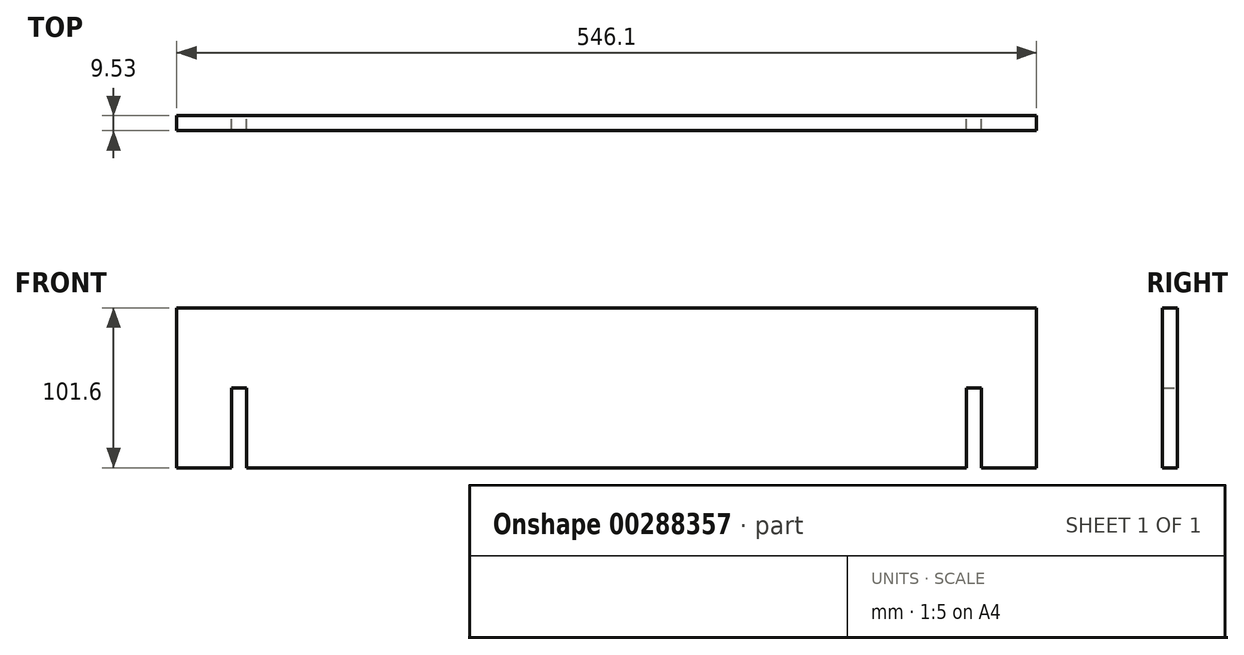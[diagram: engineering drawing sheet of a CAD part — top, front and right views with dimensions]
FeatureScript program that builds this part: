
annotation { "Feature Type Name" : "Feature", "Feature Type Description" : "" }
export const myFeature = defineFeature(function(context is Context, id is Id, definition is map)
    precondition{}
    {
        {
            var Q0;
            Q0=qCreatedBy(makeId("Front.planeOp"),FACE);
            var sketch = newSketch(context, id + "F0", { "sketchPlane" : qUnion([Q0])});
            skLineSegment(sketch, "E0.bottom", {"start": v(-273.05, -50.8) * mm, "end": v(-238.12, -50.8) * mm});
            skLineSegment(sketch, "E0.top", {"start": v(-273.05, 50.8) * mm, "end": v(273.05, 50.8) * mm});
            skLineSegment(sketch, "E0.left", {"start": v(-273.05, -50.8) * mm, "end": v(-273.05, 50.8) * mm});
            skLineSegment(sketch, "E0.right", {"start": v(273.05, -50.8) * mm, "end": v(273.05, 50.8) * mm});
            skPoint(sketch, "E0.middle", {"position": v(0, 0) * mm});
            skLineSegment(sketch, "E1.top", {"start": v(-238.12, 0) * mm, "end": v(-228.6, 0) * mm});
            skLineSegment(sketch, "E1.left", {"start": v(-238.12, -50.8) * mm, "end": v(-238.12, 0) * mm});
            skLineSegment(sketch, "E1.right", {"start": v(-228.6, -50.8) * mm, "end": v(-228.6, 0) * mm});
            skLineSegment(sketch, "E2.trimOffspring", {"start": v(-228.6, -50.8) * mm, "end": v(228.6, -50.8) * mm});
            skLineSegment(sketch, "E3.top", {"start": v(228.6, 0) * mm, "end": v(238.12, 0) * mm});
            skLineSegment(sketch, "E3.left", {"start": v(228.6, -50.8) * mm, "end": v(228.6, 0) * mm});
            skLineSegment(sketch, "E3.right", {"start": v(238.12, -50.8) * mm, "end": v(238.12, 0) * mm});
            skLineSegment(sketch, "E4.trimOffspring", {"start": v(238.12, -50.8) * mm, "end": v(273.05, -50.8) * mm});
            skSolve(sketch);
        }
        {
            var Q0;
            Q0 = qSketchRegion(id + "F0", true);
            extrude(context, id + "F1", {"entities" : qUnion([Q0]), "depth" : 9.52 * mm});
        }
    });
